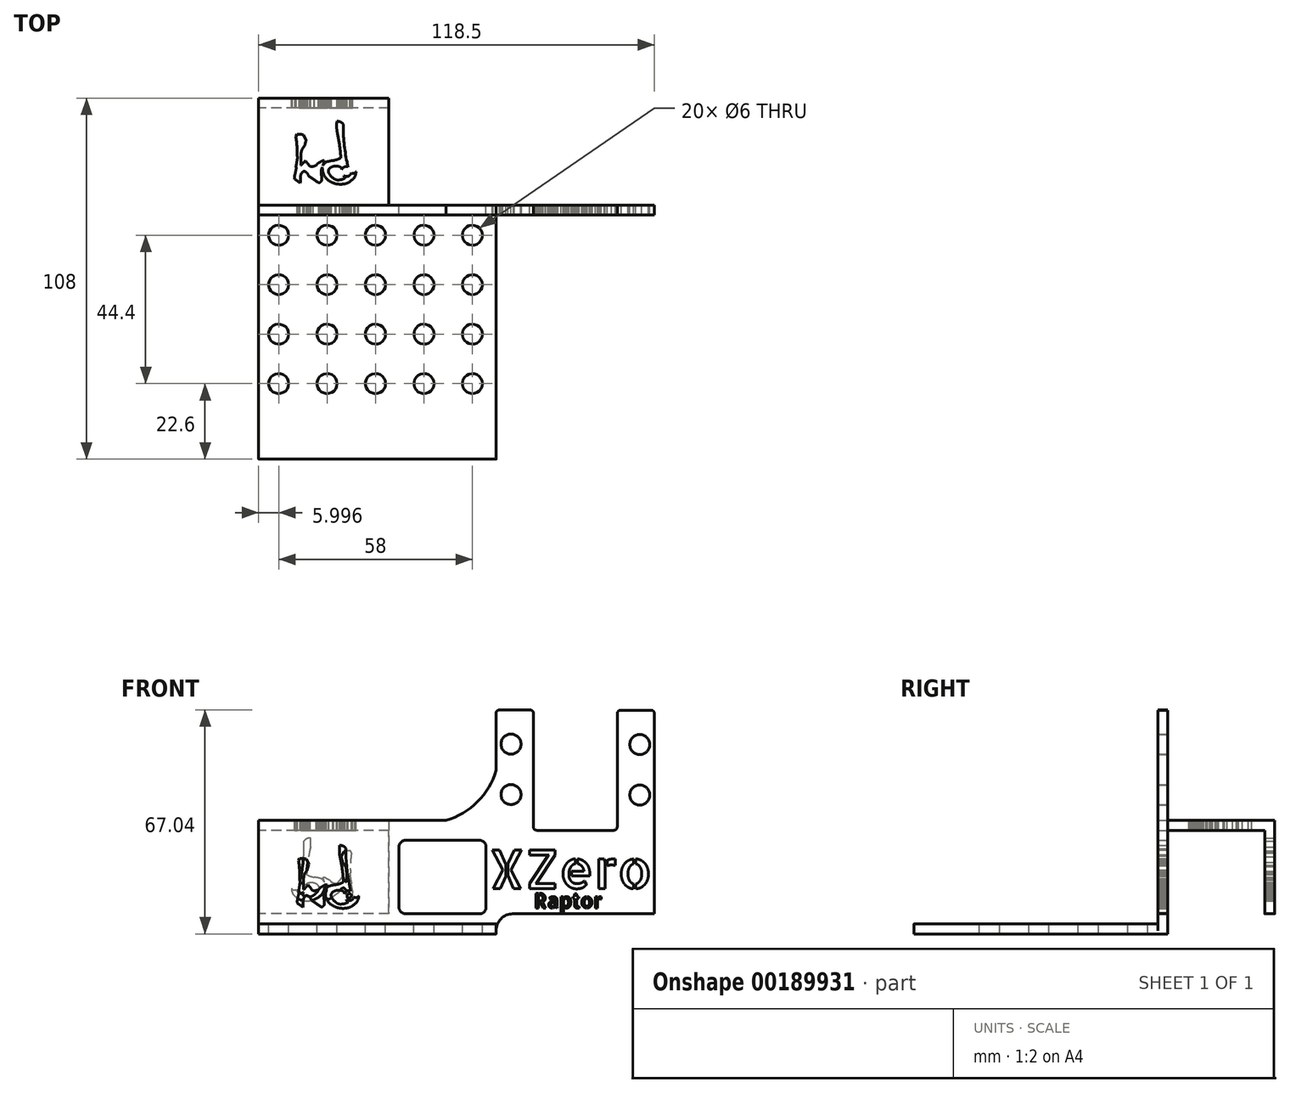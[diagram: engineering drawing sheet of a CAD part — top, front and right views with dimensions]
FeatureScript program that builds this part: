
annotation { "Feature Type Name" : "Feature", "Feature Type Description" : "" }
export const myFeature = defineFeature(function(context is Context, id is Id, definition is map)
    precondition{}
    {
        {
            var Q0;
            Q0=qCreatedBy(makeId("Front.planeOp"),FACE);
            var sketch = newSketch(context, id + "F0", { "sketchPlane" : qUnion([Q0])});
            skLineSegment(sketch, "E0", {"start": v(22.39, 29.47) * mm, "end": v(22.39, 4.47) * mm});
            skLineSegment(sketch, "E1", {"start": v(22.39, 29.47) * mm, "end": v(22.39, 64.37) * mm});
            skLineSegment(sketch, "E2", {"start": v(10.24, 29.47) * mm, "end": v(-12.86, 29.47) * mm});
            skLineSegment(sketch, "E3", {"start": v(-25.01, 47.47) * mm, "end": v(-25.01, 64.5) * mm});
            skLineSegment(sketch, "E4", {"start": v(-25.01, 4.47) * mm, "end": v(22.39, 4.47) * mm});
            skLineSegment(sketch, "E5", {"start": v(-24.01, 65.5) * mm, "end": v(-14.86, 65.5) * mm});
            skLineSegment(sketch, "E6", {"start": v(-13.86, 64.5) * mm, "end": v(-13.86, 30.47) * mm});
            skLineSegment(sketch, "E7", {"start": v(11.24, 64.37) * mm, "end": v(11.24, 30.47) * mm});
            skLineSegment(sketch, "E8", {"start": v(12.24, 65.37) * mm, "end": v(21.39, 65.37) * mm});
            skLineSegment(sketch, "E9", {"start": v(22.39, 2.47) * mm, "end": v(22.39, 4.47) * mm});
            skPoint(sketch, "E10.centerSnap0", {"position": v(-19.44, 65.5) * mm});
            skPoint(sketch, "E11.centerSnap0", {"position": v(16.81, 65.37) * mm});
            skPoint(sketch, "E12.visualSharp", {"position": v(-25.01, 65.5) * mm});
            skArc(sketch, "E12.filletArc", {"start": v(-24.01, 65.5) * mm, "mid": v(-24.72, 65.22) * mm, "end": v(-25.01, 64.5) * mm});
            skPoint(sketch, "E13.visualSharp", {"position": v(-13.86, 65.5) * mm});
            skArc(sketch, "E13.filletArc", {"start": v(-13.86, 64.5) * mm, "mid": v(-14.16, 65.22) * mm, "end": v(-14.86, 65.5) * mm});
            skPoint(sketch, "E14.visualSharp", {"position": v(11.24, 65.37) * mm});
            skArc(sketch, "E14.filletArc", {"start": v(12.24, 65.37) * mm, "mid": v(11.53, 65.08) * mm, "end": v(11.24, 64.37) * mm});
            skPoint(sketch, "E15.visualSharp", {"position": v(22.39, 65.37) * mm});
            skArc(sketch, "E15.filletArc", {"start": v(22.39, 64.37) * mm, "mid": v(22.1, 65.08) * mm, "end": v(21.39, 65.37) * mm});
            skPoint(sketch, "E16.visualSharp", {"position": v(-13.86, 29.47) * mm});
            skArc(sketch, "E16.filletArc", {"start": v(-13.86, 30.47) * mm, "mid": v(-13.57, 29.76) * mm, "end": v(-12.86, 29.47) * mm});
            skPoint(sketch, "E17.visualSharp", {"position": v(11.24, 29.47) * mm});
            skArc(sketch, "E17.filletArc", {"start": v(10.24, 29.47) * mm, "mid": v(10.94, 29.76) * mm, "end": v(11.24, 30.47) * mm});
            skPoint(sketch, "E18.visualSharp", {"position": v(-25.01, 1.47) * mm});
            skPoint(sketch, "E19.visualSharp", {"position": v(22.39, 1.47) * mm});
            skArc(sketch, "E19.filletArc", {"start": v(21.39, 1.47) * mm, "mid": v(22.1, 1.76) * mm, "end": v(22.39, 2.47) * mm});
            skLineSegment(sketch, "E20", {"start": v(-17.56, 55.26) * mm, "end": v(-17.61, 55.26) * mm});
            skLineSegment(sketch, "E21", {"start": v(-23.56, 55.26) * mm, "end": v(-23.51, 55.26) * mm});
            skCircle(sketch, "E22", {"center": v(-20.56, 55.26) * mm, "radius": 3 * mm});
            skCircle(sketch, "E23", {"center": v(17.98, 55.12) * mm, "radius": 3 * mm});
            skPoint(sketch, "E24.end.orphan", {"position": v(20.98, 55.12) * mm});
            skPoint(sketch, "E24.start.orphan", {"position": v(22.39, 55.12) * mm});
            skPoint(sketch, "E25.end.orphan", {"position": v(14.98, 55.12) * mm});
            skPoint(sketch, "E26.orphan", {"position": v(-25.01, 55.26) * mm});
            skCircle(sketch, "E27", {"center": v(-20.56, 40.16) * mm, "radius": 3 * mm});
            skCircle(sketch, "E28", {"center": v(17.98, 40.02) * mm, "radius": 3 * mm});
            skLineSegment(sketch, "E29", {"start": v(-57.11, 29.47) * mm, "end": v(-96.11, 29.47) * mm});
            skLineSegment(sketch, "E30", {"start": v(-96.11, 1.47) * mm, "end": v(-96.11, 29.47) * mm});
            skLineSegment(sketch, "E31.0", {"start": v(-30.01, 4.47) * mm, "end": v(-52.11, 4.47) * mm});
            skLineSegment(sketch, "E31.1", {"start": v(-54.11, 24.47) * mm, "end": v(-54.11, 6.47) * mm});
            skLineSegment(sketch, "E31.2", {"start": v(-30.01, 26.47) * mm, "end": v(-52.11, 26.47) * mm});
            skLineSegment(sketch, "E31.3", {"start": v(-28.01, 24.47) * mm, "end": v(-28.01, 6.47) * mm});
            skLineSegment(sketch, "E32", {"start": v(-96.11, -1.53) * mm, "end": v(-96.11, 1.47) * mm});
            skLineSegment(sketch, "E33", {"start": v(-96.11, 29.47) * mm, "end": v(-96.11, 32.47) * mm});
            skLineSegment(sketch, "E34", {"start": v(-96.11, 32.47) * mm, "end": v(-57.11, 32.47) * mm});
            skLineSegment(sketch, "E35", {"start": v(-57.11, 32.47) * mm, "end": v(-57.11, 29.47) * mm});
            skLineSegment(sketch, "E36", {"start": v(-25.01, 4.47) * mm, "end": v(-25.01, 1.47) * mm});
            skText(sketch, "E37", { "text": "XZero", "fontName": "AllertaStencil-Regular.ttf"});
            skPoint(sketch, "E38.visualSharp", {"position": v(-54.11, 26.47) * mm});
            skArc(sketch, "E38.filletArc", {"start": v(-52.11, 26.47) * mm, "mid": v(-53.53, 25.88) * mm, "end": v(-54.11, 24.47) * mm});
            skPoint(sketch, "E39.visualSharp", {"position": v(-28.01, 26.47) * mm});
            skArc(sketch, "E39.filletArc", {"start": v(-28.01, 24.47) * mm, "mid": v(-28.6, 25.88) * mm, "end": v(-30.01, 26.47) * mm});
            skPoint(sketch, "E40.visualSharp", {"position": v(-54.11, 4.47) * mm});
            skArc(sketch, "E40.filletArc", {"start": v(-54.11, 6.47) * mm, "mid": v(-53.53, 5.05) * mm, "end": v(-52.11, 4.47) * mm});
            skPoint(sketch, "E41.visualSharp", {"position": v(-28.01, 4.47) * mm});
            skArc(sketch, "E41.filletArc", {"start": v(-30.01, 4.47) * mm, "mid": v(-28.6, 5.05) * mm, "end": v(-28.01, 6.47) * mm});
            skLineSegment(sketch, "E42", {"start": v(-25.01, 1.47) * mm, "end": v(-25.01, -1.53) * mm});
            skLineSegment(sketch, "E43", {"start": v(-96.11, -1.53) * mm, "end": v(-25.01, -1.53) * mm});
            skText(sketch, "E44", { "text": "Raptor", "fontName": "AllertaStencil-Regular.ttf"});
            skArc(sketch, "E45", {"start": v(-83.84, 14.55) * mm, "mid": v(-83.85, 17.48) * mm, "end": v(-84.16, 20.4) * mm});
            skLineSegment(sketch, "E46", {"start": v(-84.16, 20.4) * mm, "end": v(-83.84, 21.04) * mm});
            skArc(sketch, "E47", {"start": v(-81.85, 20.88) * mm, "mid": v(-82.84, 21.04) * mm, "end": v(-83.84, 21.04) * mm});
            skLineSegment(sketch, "E48", {"start": v(-81.85, 20.88) * mm, "end": v(-81.1, 19.28) * mm});
            skArc(sketch, "E49", {"start": v(-81.1, 19.28) * mm, "mid": v(-81.32, 18.44) * mm, "end": v(-81.54, 17.6) * mm});
            skArc(sketch, "E50", {"start": v(-81.54, 17.6) * mm, "mid": v(-81.98, 17) * mm, "end": v(-82.38, 16.39) * mm});
            skArc(sketch, "E51", {"start": v(-82.38, 16.39) * mm, "mid": v(-82.56, 15.71) * mm, "end": v(-82.66, 15.02) * mm});
            skArc(sketch, "E52", {"start": v(-82.66, 15.02) * mm, "mid": v(-82.7, 13.37) * mm, "end": v(-82.66, 11.71) * mm});
            skArc(sketch, "E53", {"start": v(-82.66, 11.71) * mm, "mid": v(-81.95, 12.42) * mm, "end": v(-81.29, 13.18) * mm});
            skArc(sketch, "E54", {"start": v(-81.29, 13.18) * mm, "mid": v(-80.58, 12.24) * mm, "end": v(-79.82, 11.34) * mm});
            skArc(sketch, "E55", {"start": v(-79.82, 11.34) * mm, "mid": v(-78.95, 11.45) * mm, "end": v(-78.12, 11.73) * mm});
            skArc(sketch, "E56", {"start": v(-78.12, 11.73) * mm, "mid": v(-77.85, 12) * mm, "end": v(-77.66, 12.34) * mm});
            skArc(sketch, "E57", {"start": v(-77.66, 12.34) * mm, "mid": v(-76.93, 12.71) * mm, "end": v(-76.22, 13.1) * mm});
            skArc(sketch, "E58", {"start": v(-75.6, 13.1) * mm, "mid": v(-75.91, 13.12) * mm, "end": v(-76.22, 13.1) * mm});
            skArc(sketch, "E59", {"start": v(-76.24, 11.3) * mm, "mid": v(-76.41, 10.74) * mm, "end": v(-76.58, 10.16) * mm});
            skArc(sketch, "E60", {"start": v(-76.58, 10.16) * mm, "mid": v(-76.6, 9.55) * mm, "end": v(-76.58, 8.95) * mm});
            skArc(sketch, "E61", {"start": v(-76.58, 8.95) * mm, "mid": v(-76.5, 8.7) * mm, "end": v(-76.42, 8.47) * mm});
            skArc(sketch, "E62", {"start": v(-76.42, 7.43) * mm, "mid": v(-76.42, 7.95) * mm, "end": v(-76.42, 8.47) * mm});
            skArc(sketch, "E63", {"start": v(-76.54, 6.93) * mm, "mid": v(-76.48, 7.18) * mm, "end": v(-76.42, 7.43) * mm});
            skArc(sketch, "E64", {"start": v(-76.54, 6.93) * mm, "mid": v(-76.83, 6.77) * mm, "end": v(-77.06, 6.54) * mm});
            skArc(sketch, "E65", {"start": v(-77.4, 6.54) * mm, "mid": v(-77.23, 6.53) * mm, "end": v(-77.06, 6.54) * mm});
            skArc(sketch, "E66", {"start": v(-77.4, 6.54) * mm, "mid": v(-78.88, 7.58) * mm, "end": v(-80.36, 8.6) * mm});
            skArc(sketch, "E67", {"start": v(-80.36, 8.6) * mm, "mid": v(-80.56, 9.1) * mm, "end": v(-80.83, 9.54) * mm});
            skArc(sketch, "E68", {"start": v(-80.83, 9.54) * mm, "mid": v(-81.28, 9.81) * mm, "end": v(-81.75, 10.07) * mm});
            skArc(sketch, "E69", {"start": v(-81.75, 10.07) * mm, "mid": v(-82.19, 9.66) * mm, "end": v(-82.6, 9.2) * mm});
            skArc(sketch, "E70", {"start": v(-82.6, 9.2) * mm, "mid": v(-82.73, 8.68) * mm, "end": v(-82.78, 8.14) * mm});
            skArc(sketch, "E71", {"start": v(-82.78, 8.14) * mm, "mid": v(-82.8, 7.51) * mm, "end": v(-82.78, 6.89) * mm});
            skArc(sketch, "E72", {"start": v(-82.87, 6.47) * mm, "mid": v(-83.68, 7.07) * mm, "end": v(-84.51, 7.63) * mm});
            skArc(sketch, "E73", {"start": v(-84.51, 8.78) * mm, "mid": v(-84.53, 8.2) * mm, "end": v(-84.51, 7.63) * mm});
            skArc(sketch, "E74", {"start": v(-84.51, 8.78) * mm, "mid": v(-84.2, 10.01) * mm, "end": v(-84, 11.27) * mm});
            skArc(sketch, "E75", {"start": v(-84, 11.27) * mm, "mid": v(-84.08, 11.3) * mm, "end": v(-84.18, 11.33) * mm});
            skArc(sketch, "E76", {"start": v(-84.18, 11.33) * mm, "mid": v(-83.96, 12.28) * mm, "end": v(-83.81, 13.23) * mm});
            skArc(sketch, "E77", {"start": v(-83.84, 14.43) * mm, "mid": v(-83.78, 14.47) * mm, "end": v(-83.72, 14.52) * mm});
            skArc(sketch, "E78", {"start": v(-83.84, 14.43) * mm, "mid": v(-83.84, 14.5) * mm, "end": v(-83.84, 14.55) * mm});
            skArc(sketch, "E79", {"start": v(-83.81, 13.23) * mm, "mid": v(-83.73, 13.63) * mm, "end": v(-83.7, 14.04) * mm});
            skArc(sketch, "E80", {"start": v(-83.7, 14.04) * mm, "mid": v(-83.68, 14.28) * mm, "end": v(-83.72, 14.52) * mm});
            skArc(sketch, "E81", {"start": v(-74.97, 12.78) * mm, "mid": v(-75.16, 12.68) * mm, "end": v(-75.35, 12.56) * mm});
            skArc(sketch, "E82", {"start": v(-73.11, 13.16) * mm, "mid": v(-74.05, 13.02) * mm, "end": v(-74.97, 12.78) * mm});
            skArc(sketch, "E83", {"start": v(-73.11, 13.16) * mm, "mid": v(-71.88, 13.46) * mm, "end": v(-70.72, 13.98) * mm});
            skArc(sketch, "E84", {"start": v(-70.72, 13.98) * mm, "mid": v(-70.8, 15.38) * mm, "end": v(-70.95, 16.77) * mm});
            skArc(sketch, "E85", {"start": v(-70.95, 16.77) * mm, "mid": v(-71.36, 19.48) * mm, "end": v(-71.89, 22.17) * mm});
            skArc(sketch, "E86", {"start": v(-71.89, 24.92) * mm, "mid": v(-71.93, 23.54) * mm, "end": v(-71.89, 22.17) * mm});
            skArc(sketch, "E87", {"start": v(-69.95, 24) * mm, "mid": v(-70.78, 24.74) * mm, "end": v(-71.89, 24.92) * mm});
            skArc(sketch, "E88", {"start": v(-69.95, 24) * mm, "mid": v(-69.73, 18.33) * mm, "end": v(-68.85, 12.74) * mm});
            skArc(sketch, "E89", {"start": v(-68.85, 12.74) * mm, "mid": v(-68.72, 12.01) * mm, "end": v(-68.56, 11.3) * mm});
            skArc(sketch, "E90", {"start": v(-68.56, 11.3) * mm, "mid": v(-69.65, 11.26) * mm, "end": v(-70.44, 10.5) * mm});
            skArc(sketch, "E91", {"start": v(-70.44, 10.5) * mm, "mid": v(-70.63, 11.05) * mm, "end": v(-71.11, 11.38) * mm});
            skArc(sketch, "E92", {"start": v(-71.11, 11.38) * mm, "mid": v(-72.07, 11.53) * mm, "end": v(-73.04, 11.42) * mm});
            skArc(sketch, "E93", {"start": v(-73.04, 11.42) * mm, "mid": v(-73.71, 11.13) * mm, "end": v(-74.25, 10.64) * mm});
            skArc(sketch, "E94", {"start": v(-74.25, 10.64) * mm, "mid": v(-74.43, 10) * mm, "end": v(-74.25, 9.37) * mm});
            skArc(sketch, "E95", {"start": v(-74.25, 9.37) * mm, "mid": v(-73.7, 8.55) * mm, "end": v(-72.95, 7.89) * mm});
            skArc(sketch, "E96", {"start": v(-72.95, 7.89) * mm, "mid": v(-72.37, 7.53) * mm, "end": v(-71.71, 7.35) * mm});
            skArc(sketch, "E97", {"start": v(-71.71, 7.35) * mm, "mid": v(-70.52, 7.5) * mm, "end": v(-69.4, 7.9) * mm});
            skArc(sketch, "E98", {"start": v(-69.84, 8.65) * mm, "mid": v(-69.64, 8.26) * mm, "end": v(-69.4, 7.9) * mm});
            skArc(sketch, "E99", {"start": v(-69.84, 8.65) * mm, "mid": v(-68.52, 8.49) * mm, "end": v(-67.6, 9.45) * mm});
            skArc(sketch, "E100", {"start": v(-67.6, 9.45) * mm, "mid": v(-67.03, 9.35) * mm, "end": v(-66.46, 9.45) * mm});
            skArc(sketch, "E101", {"start": v(-66.46, 9.45) * mm, "mid": v(-66.3, 9.62) * mm, "end": v(-66.19, 9.84) * mm});
            skArc(sketch, "E102", {"start": v(-67.2, 7.52) * mm, "mid": v(-66.42, 8.56) * mm, "end": v(-66.19, 9.84) * mm});
            skArc(sketch, "E103", {"start": v(-69.85, 6.17) * mm, "mid": v(-68.41, 6.62) * mm, "end": v(-67.2, 7.52) * mm});
            skArc(sketch, "E104", {"start": v(-72.92, 6.43) * mm, "mid": v(-71.4, 6.12) * mm, "end": v(-69.85, 6.17) * mm});
            skArc(sketch, "E105", {"start": v(-75.33, 8.1) * mm, "mid": v(-74.22, 7.12) * mm, "end": v(-72.92, 6.43) * mm});
            skLineSegment(sketch, "E106", {"start": v(-82.78, 6.89) * mm, "end": v(-82.87, 6.47) * mm});
            skArc(sketch, "E107", {"start": v(-76.24, 11.3) * mm, "mid": v(-76.03, 9.64) * mm, "end": v(-75.33, 8.1) * mm});
            skArc(sketch, "E108", {"start": v(-75.35, 12.56) * mm, "mid": v(-75.76, 12.16) * mm, "end": v(-76.08, 11.68) * mm});
            skArc(sketch, "E109", {"start": v(-75.6, 13.1) * mm, "mid": v(-75.85, 12.4) * mm, "end": v(-76.08, 11.68) * mm});
            skLineSegment(sketch, "E110", {"start": v(-57.11, 32.47) * mm, "end": v(-40.05, 32.47) * mm});
            skCircle(sketch, "E111.0", {"center": v(-69.01, 9.88) * mm, "radius": 0.65 * mm});
            skArc(sketch, "E112", {"start": v(-40.05, 32.47) * mm, "mid": v(-30.57, 38) * mm, "end": v(-25.01, 47.47) * mm});
            skPoint(sketch, "E113.end.orphan", {"position": v(-25.01, 29.47) * mm});
            skLineSegment(sketch, "E114", {"start": v(-25.01, 1.47) * mm, "end": v(-96.11, 1.47) * mm});
            const initialGuessF0  = {"E37": [-0.02729, 0.012, 1, 0, 0.01158], "E44": [-0.01363, 0.00623, 1, 0, 0.00439]};
            skSetInitialGuess(sketch, initialGuessF0);
            skSolve(sketch);
        }
        {
            var Q0;
            Q0=makeQuery(id+"F0.imprint","IMPRINT",FACE,{"disambiguationData":[TD([[makeQuery(id+"F0.imprint","IMPRINT",EDGE,{"derivedFrom":sQuery(id+"F0.wireOp",EDGE,"E0")}),-1.0]])]});
            var Q1;
            Q1=makeQuery(id+"F0.imprint","IMPRINT",FACE,{"disambiguationData":[TD([[makeQuery(id+"F0.imprint","IMPRINT",EDGE,{"derivedFrom":sQuery(id+"F0.wireOp",EDGE,"E4")}),-1.0]])]});
            var Q2;
            Q2=makeQuery(id+"F0.imprint","IMPRINT",FACE,{"disambiguationData":[TD([[makeQuery(id+"F0.imprint","IMPRINT",EDGE,{"derivedFrom":sQuery(id+"F0.wireOp",EDGE,"E29")}),1.0]])]});
            var Q3;
            {var subQ3=sQuery(id+"F0.wireOp",EDGE,"46Qzlj7U-cznB-aaa3-vZE3-pz9t5rDoRomK");Q3=makeQuery(id+"F0.imprint","IMPRINT",FACE,{"disambiguationData":[TD([[makeQuery(id+"F0.imprint","IMPRINT",EDGE,{"derivedFrom":subQ3}),-1.0]])]});}
            var Q4;
            {var subQ0=sQuery(id+"F0.wireOp",EDGE,"E37.sketch_text.stroke-6");var subQ1=sQuery(id+"F0.wireOp",EDGE,"46Qzlj7U-cznB-aaa3-vZE3-pz9t5rDoRomK");var subQ2=makeQuery(id+"F0.imprint","INTERSECT",VERTEX,{"derivedFrom":[subQ1,subQ0]});Q4=makeQuery(id+"F0.imprint","IMPRINT",FACE,{"disambiguationData":[TD([[makeQuery(id+"F0.imprint","IMPRINT",EDGE,{"disambiguationData":[TD([[subQ2,-1.0]])],"derivedFrom":subQ1}),1.0]])]});}
            var Q5;
            {var subQ0=sQuery(id+"F0.wireOp",EDGE,"idUH9Glq-0qPq-0oZk-nQ6q-rgwbrYVED9FP");Q5=makeQuery(id+"F0.imprint","IMPRINT",FACE,{"disambiguationData":[TD([[makeQuery(id+"F0.imprint","IMPRINT",EDGE,{"derivedFrom":subQ0}),-1.0]])]});}
            extrude(context, id + "F1", {"entities" : qUnion([Q0, Q1, Q2, Q3, Q4, Q5]), "depth" : 3 * mm});
        }
        {
            var Q0;
            Q0=makeQuery(id+"F0.imprint","IMPRINT",FACE,{"disambiguationData":[TD([[makeQuery(id+"F0.imprint","IMPRINT",EDGE,{"derivedFrom":sQuery(id+"F0.wireOp",EDGE,"E29")}),-1.0]])]});
            extrude(context, id + "F2", {"entities" : qUnion([Q0]), "operationType" : NewBodyOperationType.ADD, "depth" : 3 * mm});
        }
        {
            var Q0;
            Q0=makeQuery(id+"F0.imprint","IMPRINT",FACE,{"disambiguationData":[TD([[makeQuery(id+"F0.imprint","IMPRINT",EDGE,{"derivedFrom":sQuery(id+"F0.wireOp",EDGE,"E29")}),-1.0]])]});
            extrude(context, id + "F3", {"entities" : qUnion([Q0]), "oppositeDirection" : true, "depth" : 29 * mm});
        }
        {
            var Q0;
            Q0=makeQuery(id+"F0.imprint","IMPRINT",FACE,{"disambiguationData":[TD([[makeQuery(id+"F0.imprint","IMPRINT",EDGE,{"derivedFrom":sQuery(id+"F0.wireOp",EDGE,"E32")}),-1.0]])]});
            extrude(context, id + "F4", {"entities" : qUnion([Q0]), "operationType" : NewBodyOperationType.ADD, "depth" : 76 * mm});
        }
        {
            var Q0;
            Q0=makeQuery(id+"F3.opExtrude","CAP_FACE",FACE,{"disambiguationData":[OSD([sQuery(id+"F0.wireOp",EDGE,"E29"),sQuery(id+"F0.wireOp",EDGE,"E33"),sQuery(id+"F0.wireOp",EDGE,"E34"),sQuery(id+"F0.wireOp",EDGE,"E35")])],"isStart":false});
            var sketch = newSketch(context, id + "F5", { "sketchPlane" : qUnion([Q0])});
            skLineSegment(sketch, "E115.0", {"start": v(96.11, 32.47) * mm, "end": v(57.11, 32.47) * mm});
            skLineSegment(sketch, "E115.1", {"start": v(57.11, 32.47) * mm, "end": v(57.11, 29.47) * mm});
            skLineSegment(sketch, "E115.2", {"start": v(57.11, 29.47) * mm, "end": v(96.11, 29.47) * mm});
            skLineSegment(sketch, "E115.3", {"start": v(96.11, 29.47) * mm, "end": v(96.11, 32.47) * mm});
            skSolve(sketch);
        }
        {
            var Q0;
            Q0=makeQuery(id+"F5.imprint","IMPRINT",FACE,{"disambiguationData":[TD([[makeQuery(id+"F5.imprint","IMPRINT",EDGE,{"derivedFrom":sQuery(id+"F5.wireOp",EDGE,"E115.0")}),1.0]])]});
            extrude(context, id + "F6", {"entities" : qUnion([Q0]), "operationType" : NewBodyOperationType.ADD, "depth" : 3 * mm});
        }
        {
            var Q0;
            Q0=makeQuery(id+"F6.boolean.opBoolean","MERGE",FACE,{"derivedFrom":[makeQuery(id+"F3.opExtrude","SWEPT_FACE",FACE,{"disambiguationData":[OSD([sQuery(id+"F0.wireOp",EDGE,"E29")])]}),makeQuery(id+"F6.opExtrude","SWEPT_FACE",FACE,{"disambiguationData":[OSD([sQuery(id+"F5.wireOp",EDGE,"E115.2")])]})]});
            var sketch = newSketch(context, id + "F7", { "sketchPlane" : qUnion([Q0])});
            skLineSegment(sketch, "E116", {"start": v(-57.11, -32) * mm, "end": v(-57.11, -29) * mm});
            skLineSegment(sketch, "E117", {"start": v(-57.11, -29) * mm, "end": v(-96.11, -29) * mm});
            skLineSegment(sketch, "E118", {"start": v(-96.11, -29) * mm, "end": v(-96.11, -32) * mm});
            skLineSegment(sketch, "E119", {"start": v(-96.11, -32) * mm, "end": v(-57.11, -32) * mm});
            skSolve(sketch);
        }
        {
            var Q0;
            Q0=makeQuery(id+"F7.imprint","IMPRINT",FACE,{"disambiguationData":[TD([[makeQuery(id+"F7.imprint","IMPRINT",EDGE,{"derivedFrom":sQuery(id+"F7.wireOp",EDGE,"E116")}),1.0]])]});
            extrude(context, id + "F8", {"entities" : qUnion([Q0]), "operationType" : NewBodyOperationType.ADD, "depth" : 25 * mm});
        }
        {
            var Q0;
            Q0=makeQuery(id+"F4.opExtrude","CAP_EDGE",EDGE,{"disambiguationData":[OSD([sQuery(id+"F0.wireOp",EDGE,"E32")])],"isStart":false});
            var Q1;
            Q1=makeQuery(id+"F4.opExtrude","CAP_EDGE",EDGE,{"disambiguationData":[OSD([sQuery(id+"F0.wireOp",EDGE,"dS1XQmwT-nCb9-MQQN-qxri-gYy9wgz1x22k")])],"isStart":false});
            var Q2;
            Q2=makeQuery(id+"F8.opExtrude","CAP_EDGE",EDGE,{"disambiguationData":[OSD([sQuery(id+"F7.wireOp",EDGE,"E118")])],"isStart":false});
            var Q3;
            Q3=makeQuery(id+"F8.opExtrude","CAP_EDGE",EDGE,{"disambiguationData":[OSD([sQuery(id+"F7.wireOp",EDGE,"E116")])],"isStart":false});
            var Q4;
            Q4=makeQuery(id+"F4.opExtrude","CAP_EDGE",EDGE,{"disambiguationData":[OSD([sQuery(id+"F0.wireOp",EDGE,"mx6WqFKt-vM0y-SFEN-eErL-Z0JPfcJ78krc")])],"isStart":true});
            var Q5;
            Q5=makeQuery(id+"F4.opExtrude","CAP_EDGE",EDGE,{"disambiguationData":[OSD([sQuery(id+"F0.wireOp",EDGE,"E36"),sQuery(id+"F0.wireOp",EDGE,"E42")])],"isStart":false});
            var Q6;
            Q6=makeQuery(id+"F1.opExtrude","SWEPT_EDGE",EDGE,{"disambiguationData":[OSD([sQuery(id+"F0.wireOp",EDGE,"E3"),sQuery(id+"F0.wireOp",EDGE,"46Qzlj7U-cznB-aaa3-vZE3-pz9t5rDoRomK"),sQuery(id+"F0.wireOp",EDGE,"idUH9Glq-0qPq-0oZk-nQ6q-rgwbrYVED9FP")])]});
            fillet(context, id + "F9", {"entities" : qUnion([Q0, Q1, Q2, Q3, Q4, Q5, Q6]), "radius" : 0.02 * mm, "tangentPropagation" : true, "allowEdgeOverflow" : false});
        }
        {
            var Q0;
            Q0=makeQuery(id+"F4.opExtrude","SWEPT_FACE",FACE,{"disambiguationData":[OSD([sQuery(id+"F0.wireOp",EDGE,"E114")])]});
            var sketch = newSketch(context, id + "F10", { "sketchPlane" : qUnion([Q0])});
            skCircle(sketch, "E120", {"center": v(-90.11, -9) * mm, "radius": 3 * mm});
            skCircle(sketch, "E121.0.1.0", {"center": v(-90.11, -23.8) * mm, "radius": 3 * mm});
            skCircle(sketch, "E121.0.2.0", {"center": v(-90.11, -38.6) * mm, "radius": 3 * mm});
            skCircle(sketch, "E121.0.3.0", {"center": v(-90.11, -53.4) * mm, "radius": 3 * mm});
            skCircle(sketch, "E121.0.4.0", {"center": v(-90.11, -68.2) * mm, "radius": 3 * mm});
            skCircle(sketch, "E121.1.0.0", {"center": v(-75.61, -9) * mm, "radius": 3 * mm});
            skCircle(sketch, "E121.1.1.0", {"center": v(-75.61, -23.8) * mm, "radius": 3 * mm});
            skCircle(sketch, "E121.1.2.0", {"center": v(-75.61, -38.6) * mm, "radius": 3 * mm});
            skCircle(sketch, "E121.1.3.0", {"center": v(-75.61, -53.4) * mm, "radius": 3 * mm});
            skCircle(sketch, "E121.1.4.0", {"center": v(-75.61, -68.2) * mm, "radius": 3 * mm});
            skCircle(sketch, "E121.2.0.0", {"center": v(-61.11, -9) * mm, "radius": 3 * mm});
            skCircle(sketch, "E121.2.1.0", {"center": v(-61.11, -23.8) * mm, "radius": 3 * mm});
            skCircle(sketch, "E121.2.2.0", {"center": v(-61.11, -38.6) * mm, "radius": 3 * mm});
            skCircle(sketch, "E121.2.3.0", {"center": v(-61.11, -53.4) * mm, "radius": 3 * mm});
            skCircle(sketch, "E121.2.4.0", {"center": v(-61.11, -68.2) * mm, "radius": 3 * mm});
            skCircle(sketch, "E121.3.0.0", {"center": v(-46.61, -9) * mm, "radius": 3 * mm});
            skCircle(sketch, "E121.3.1.0", {"center": v(-46.61, -23.8) * mm, "radius": 3 * mm});
            skCircle(sketch, "E121.3.2.0", {"center": v(-46.61, -38.6) * mm, "radius": 3 * mm});
            skCircle(sketch, "E121.3.3.0", {"center": v(-46.61, -53.4) * mm, "radius": 3 * mm});
            skCircle(sketch, "E121.3.4.0", {"center": v(-46.61, -68.2) * mm, "radius": 3 * mm});
            skCircle(sketch, "E121.4.0.0", {"center": v(-32.11, -9) * mm, "radius": 3 * mm});
            skCircle(sketch, "E121.4.1.0", {"center": v(-32.11, -23.8) * mm, "radius": 3 * mm});
            skCircle(sketch, "E121.4.2.0", {"center": v(-32.11, -38.6) * mm, "radius": 3 * mm});
            skCircle(sketch, "E121.4.3.0", {"center": v(-32.11, -53.4) * mm, "radius": 3 * mm});
            skCircle(sketch, "E121.4.4.0", {"center": v(-32.11, -68.2) * mm, "radius": 3 * mm});
            skLineSegment(sketch, "E121.direction1", {"start": v(-90.11, -9) * mm, "end": v(-75.61, -9) * mm, "construction": true});
            skLineSegment(sketch, "E121.direction2", {"start": v(-90.11, -9) * mm, "end": v(-90.11, -23.8) * mm, "construction": true});
            skSolve(sketch);
        }
        {
            var Q0;
            Q0=makeQuery(id+"F6.boolean.opBoolean","MERGE",FACE,{"derivedFrom":[makeQuery(id+"F3.opExtrude","SWEPT_FACE",FACE,{"disambiguationData":[OSD([sQuery(id+"F0.wireOp",EDGE,"E34")])]}),makeQuery(id+"F6.opExtrude","SWEPT_FACE",FACE,{"disambiguationData":[OSD([sQuery(id+"F5.wireOp",EDGE,"E115.0")])]})]});
            var sketch = newSketch(context, id + "F11", { "sketchPlane" : qUnion([Q0])});
            skArc(sketch, "E122", {"start": v(-84.64, 14.69) * mm, "mid": v(-84.65, 17.62) * mm, "end": v(-84.97, 20.53) * mm});
            skLineSegment(sketch, "E123", {"start": v(-84.97, 20.53) * mm, "end": v(-84.64, 21.18) * mm});
            skArc(sketch, "E124", {"start": v(-82.65, 21.01) * mm, "mid": v(-83.64, 21.18) * mm, "end": v(-84.64, 21.18) * mm});
            skLineSegment(sketch, "E125", {"start": v(-82.65, 21.01) * mm, "end": v(-81.9, 19.41) * mm});
            skArc(sketch, "E126", {"start": v(-81.9, 19.41) * mm, "mid": v(-82.12, 18.58) * mm, "end": v(-82.35, 17.74) * mm});
            skArc(sketch, "E127", {"start": v(-82.35, 17.74) * mm, "mid": v(-82.78, 17.14) * mm, "end": v(-83.18, 16.53) * mm});
            skArc(sketch, "E128", {"start": v(-83.18, 16.53) * mm, "mid": v(-83.36, 15.85) * mm, "end": v(-83.46, 15.16) * mm});
            skArc(sketch, "E129", {"start": v(-83.46, 15.16) * mm, "mid": v(-83.5, 13.5) * mm, "end": v(-83.46, 11.85) * mm});
            skArc(sketch, "E130", {"start": v(-83.46, 11.85) * mm, "mid": v(-82.75, 12.56) * mm, "end": v(-82.1, 13.32) * mm});
            skArc(sketch, "E131", {"start": v(-82.1, 13.32) * mm, "mid": v(-81.39, 12.37) * mm, "end": v(-80.62, 11.48) * mm});
            skArc(sketch, "E132", {"start": v(-80.62, 11.48) * mm, "mid": v(-79.75, 11.59) * mm, "end": v(-78.93, 11.87) * mm});
            skArc(sketch, "E133", {"start": v(-78.93, 11.87) * mm, "mid": v(-78.66, 12.15) * mm, "end": v(-78.46, 12.48) * mm});
            skArc(sketch, "E134", {"start": v(-78.46, 12.48) * mm, "mid": v(-77.73, 12.85) * mm, "end": v(-77.02, 13.25) * mm});
            skArc(sketch, "E135", {"start": v(-76.4, 13.25) * mm, "mid": v(-76.71, 13.26) * mm, "end": v(-77.02, 13.25) * mm});
            skArc(sketch, "E136", {"start": v(-77.04, 11.44) * mm, "mid": v(-77.22, 10.87) * mm, "end": v(-77.38, 10.3) * mm});
            skArc(sketch, "E137", {"start": v(-77.38, 10.3) * mm, "mid": v(-77.41, 9.7) * mm, "end": v(-77.38, 9.08) * mm});
            skArc(sketch, "E138", {"start": v(-77.38, 9.08) * mm, "mid": v(-77.3, 8.85) * mm, "end": v(-77.22, 8.6) * mm});
            skArc(sketch, "E139", {"start": v(-77.22, 7.57) * mm, "mid": v(-77.22, 8.1) * mm, "end": v(-77.22, 8.6) * mm});
            skArc(sketch, "E140", {"start": v(-77.35, 7.07) * mm, "mid": v(-77.28, 7.32) * mm, "end": v(-77.22, 7.57) * mm});
            skArc(sketch, "E141", {"start": v(-77.35, 7.07) * mm, "mid": v(-77.63, 6.9) * mm, "end": v(-77.86, 6.68) * mm});
            skArc(sketch, "E142", {"start": v(-78.2, 6.68) * mm, "mid": v(-78.04, 6.66) * mm, "end": v(-77.86, 6.68) * mm});
            skArc(sketch, "E143", {"start": v(-78.2, 6.68) * mm, "mid": v(-79.68, 7.72) * mm, "end": v(-81.16, 8.74) * mm});
            skArc(sketch, "E144", {"start": v(-81.16, 8.74) * mm, "mid": v(-81.36, 9.23) * mm, "end": v(-81.63, 9.68) * mm});
            skArc(sketch, "E145", {"start": v(-81.63, 9.68) * mm, "mid": v(-82.09, 9.95) * mm, "end": v(-82.55, 10.2) * mm});
            skArc(sketch, "E146", {"start": v(-82.55, 10.2) * mm, "mid": v(-83, 9.8) * mm, "end": v(-83.4, 9.35) * mm});
            skArc(sketch, "E147", {"start": v(-83.4, 9.35) * mm, "mid": v(-83.53, 8.82) * mm, "end": v(-83.58, 8.28) * mm});
            skArc(sketch, "E148", {"start": v(-83.58, 8.28) * mm, "mid": v(-83.6, 7.65) * mm, "end": v(-83.58, 7.02) * mm});
            skArc(sketch, "E149", {"start": v(-83.67, 6.6) * mm, "mid": v(-84.48, 7.2) * mm, "end": v(-85.32, 7.76) * mm});
            skArc(sketch, "E150", {"start": v(-85.32, 8.92) * mm, "mid": v(-85.33, 8.34) * mm, "end": v(-85.32, 7.76) * mm});
            skArc(sketch, "E151", {"start": v(-85.32, 8.92) * mm, "mid": v(-85, 10.15) * mm, "end": v(-84.8, 11.4) * mm});
            skArc(sketch, "E152", {"start": v(-84.8, 11.4) * mm, "mid": v(-84.88, 11.44) * mm, "end": v(-84.98, 11.47) * mm});
            skArc(sketch, "E153", {"start": v(-84.98, 11.47) * mm, "mid": v(-84.77, 12.41) * mm, "end": v(-84.62, 13.37) * mm});
            skArc(sketch, "E154", {"start": v(-84.64, 14.57) * mm, "mid": v(-84.58, 14.6) * mm, "end": v(-84.53, 14.65) * mm});
            skArc(sketch, "E155", {"start": v(-84.64, 14.57) * mm, "mid": v(-84.64, 14.63) * mm, "end": v(-84.64, 14.69) * mm});
            skArc(sketch, "E156", {"start": v(-84.62, 13.37) * mm, "mid": v(-84.53, 13.77) * mm, "end": v(-84.5, 14.17) * mm});
            skArc(sketch, "E157", {"start": v(-84.5, 14.17) * mm, "mid": v(-84.48, 14.41) * mm, "end": v(-84.53, 14.65) * mm});
            skArc(sketch, "E158", {"start": v(-75.77, 12.92) * mm, "mid": v(-75.97, 12.82) * mm, "end": v(-76.15, 12.7) * mm});
            skArc(sketch, "E159", {"start": v(-73.92, 13.3) * mm, "mid": v(-74.86, 13.16) * mm, "end": v(-75.77, 12.92) * mm});
            skArc(sketch, "E160", {"start": v(-73.92, 13.3) * mm, "mid": v(-72.68, 13.6) * mm, "end": v(-71.52, 14.11) * mm});
            skArc(sketch, "E161", {"start": v(-71.52, 14.11) * mm, "mid": v(-71.6, 15.52) * mm, "end": v(-71.75, 16.91) * mm});
            skArc(sketch, "E162", {"start": v(-71.75, 16.91) * mm, "mid": v(-72.16, 19.62) * mm, "end": v(-72.69, 22.3) * mm});
            skArc(sketch, "E163", {"start": v(-72.69, 25.05) * mm, "mid": v(-72.73, 23.68) * mm, "end": v(-72.69, 22.3) * mm});
            skArc(sketch, "E164", {"start": v(-70.76, 24.13) * mm, "mid": v(-71.59, 24.87) * mm, "end": v(-72.69, 25.05) * mm});
            skArc(sketch, "E165", {"start": v(-70.76, 24.13) * mm, "mid": v(-70.53, 18.47) * mm, "end": v(-69.66, 12.87) * mm});
            skArc(sketch, "E166", {"start": v(-69.66, 12.87) * mm, "mid": v(-69.52, 12.15) * mm, "end": v(-69.36, 11.43) * mm});
            skArc(sketch, "E167", {"start": v(-69.36, 11.43) * mm, "mid": v(-70.45, 11.4) * mm, "end": v(-71.25, 10.65) * mm});
            skArc(sketch, "E168", {"start": v(-71.25, 10.65) * mm, "mid": v(-71.44, 11.19) * mm, "end": v(-71.91, 11.51) * mm});
            skArc(sketch, "E169", {"start": v(-71.91, 11.51) * mm, "mid": v(-72.88, 11.67) * mm, "end": v(-73.84, 11.56) * mm});
            skArc(sketch, "E170", {"start": v(-73.84, 11.56) * mm, "mid": v(-74.51, 11.27) * mm, "end": v(-75.06, 10.78) * mm});
            skArc(sketch, "E171", {"start": v(-75.06, 10.78) * mm, "mid": v(-75.24, 10.14) * mm, "end": v(-75.06, 9.5) * mm});
            skArc(sketch, "E172", {"start": v(-75.06, 9.5) * mm, "mid": v(-74.5, 8.68) * mm, "end": v(-73.75, 8.02) * mm});
            skArc(sketch, "E173", {"start": v(-73.75, 8.02) * mm, "mid": v(-73.17, 7.66) * mm, "end": v(-72.51, 7.49) * mm});
            skArc(sketch, "E174", {"start": v(-72.51, 7.49) * mm, "mid": v(-71.33, 7.63) * mm, "end": v(-70.2, 8.03) * mm});
            skArc(sketch, "E175", {"start": v(-70.64, 8.8) * mm, "mid": v(-70.44, 8.4) * mm, "end": v(-70.2, 8.03) * mm});
            skArc(sketch, "E176", {"start": v(-70.64, 8.8) * mm, "mid": v(-69.32, 8.62) * mm, "end": v(-68.4, 9.59) * mm});
            skArc(sketch, "E177", {"start": v(-68.4, 9.59) * mm, "mid": v(-67.83, 9.5) * mm, "end": v(-67.27, 9.59) * mm});
            skArc(sketch, "E178", {"start": v(-67.27, 9.59) * mm, "mid": v(-67.1, 9.76) * mm, "end": v(-66.99, 9.97) * mm});
            skArc(sketch, "E179", {"start": v(-68, 7.66) * mm, "mid": v(-67.22, 8.7) * mm, "end": v(-66.99, 9.97) * mm});
            skArc(sketch, "E180", {"start": v(-70.65, 6.3) * mm, "mid": v(-69.22, 6.76) * mm, "end": v(-68, 7.66) * mm});
            skArc(sketch, "E181", {"start": v(-73.72, 6.57) * mm, "mid": v(-72.2, 6.26) * mm, "end": v(-70.65, 6.3) * mm});
            skArc(sketch, "E182", {"start": v(-76.13, 8.24) * mm, "mid": v(-75.03, 7.26) * mm, "end": v(-73.72, 6.57) * mm});
            skLineSegment(sketch, "E183", {"start": v(-83.58, 7.02) * mm, "end": v(-83.67, 6.6) * mm});
            skArc(sketch, "E184", {"start": v(-75.77, 12.92) * mm, "mid": v(-75.97, 12.81) * mm, "end": v(-76.15, 12.7) * mm});
            skArc(sketch, "E185", {"start": v(-77.04, 11.44) * mm, "mid": v(-76.83, 9.77) * mm, "end": v(-76.13, 8.24) * mm});
            skArc(sketch, "E186", {"start": v(-76.15, 12.7) * mm, "mid": v(-76.56, 12.3) * mm, "end": v(-76.89, 11.82) * mm});
            skArc(sketch, "E187", {"start": v(-76.4, 13.25) * mm, "mid": v(-76.65, 12.53) * mm, "end": v(-76.89, 11.82) * mm});
            skCircle(sketch, "E188.0", {"center": v(-69.81, 10.02) * mm, "radius": 0.65 * mm});
            skSolve(sketch);
        }
        {
            var Q0;
            Q0=makeQuery(id+"F11.imprint","IMPRINT",FACE,{"disambiguationData":[TD([[makeQuery(id+"F11.imprint","IMPRINT",EDGE,{"derivedFrom":sQuery(id+"F11.wireOp",EDGE,"E122")}),-1.0]])]});
            var Q1;
            Q1=makeQuery(id+"F11.imprint","IMPRINT",FACE,{"disambiguationData":[TD([[makeQuery(id+"F11.imprint","IMPRINT",EDGE,{"derivedFrom":sQuery(id+"F11.wireOp",EDGE,"e9a27ff7-29ba-4c5a-bb0c-0f35ec83b421")}),1.0]])]});
            extrude(context, id + "F12", {"entities" : qUnion([Q0, Q1]), "operationType" : NewBodyOperationType.REMOVE, "oppositeDirection" : true, "depth" : 3 * mm});
        }
        {
            var Q0;
            Q0=makeQuery(id+"F10.imprint","IMPRINT",FACE,{"disambiguationData":[TD([[makeQuery(id+"F10.imprint","IMPRINT",EDGE,{"derivedFrom":sQuery(id+"F10.wireOp",EDGE,"E120")}),1.0]])]});
            var Q1;
            Q1=makeQuery(id+"F10.imprint","IMPRINT",FACE,{"disambiguationData":[TD([[makeQuery(id+"F10.imprint","IMPRINT",EDGE,{"derivedFrom":sQuery(id+"F10.wireOp",EDGE,"E121.1.0.0")}),1.0]])]});
            var Q2;
            Q2=makeQuery(id+"F10.imprint","IMPRINT",FACE,{"disambiguationData":[TD([[makeQuery(id+"F10.imprint","IMPRINT",EDGE,{"derivedFrom":sQuery(id+"F10.wireOp",EDGE,"E121.2.0.0")}),1.0]])]});
            var Q3;
            Q3=makeQuery(id+"F10.imprint","IMPRINT",FACE,{"disambiguationData":[TD([[makeQuery(id+"F10.imprint","IMPRINT",EDGE,{"derivedFrom":sQuery(id+"F10.wireOp",EDGE,"E121.4.0.0")}),1.0]])]});
            var Q4;
            Q4=makeQuery(id+"F10.imprint","IMPRINT",FACE,{"disambiguationData":[TD([[makeQuery(id+"F10.imprint","IMPRINT",EDGE,{"derivedFrom":sQuery(id+"F10.wireOp",EDGE,"E121.4.1.0")}),1.0]])]});
            var Q5;
            Q5=makeQuery(id+"F10.imprint","IMPRINT",FACE,{"disambiguationData":[TD([[makeQuery(id+"F10.imprint","IMPRINT",EDGE,{"derivedFrom":sQuery(id+"F10.wireOp",EDGE,"E121.3.1.0")}),1.0]])]});
            var Q6;
            Q6=makeQuery(id+"F10.imprint","IMPRINT",FACE,{"disambiguationData":[TD([[makeQuery(id+"F10.imprint","IMPRINT",EDGE,{"derivedFrom":sQuery(id+"F10.wireOp",EDGE,"E121.3.2.0")}),1.0]])]});
            var Q7;
            Q7=makeQuery(id+"F10.imprint","IMPRINT",FACE,{"disambiguationData":[TD([[makeQuery(id+"F10.imprint","IMPRINT",EDGE,{"derivedFrom":sQuery(id+"F10.wireOp",EDGE,"E121.4.2.0")}),1.0]])]});
            var Q8;
            Q8=makeQuery(id+"F10.imprint","IMPRINT",FACE,{"disambiguationData":[TD([[makeQuery(id+"F10.imprint","IMPRINT",EDGE,{"derivedFrom":sQuery(id+"F10.wireOp",EDGE,"E121.4.3.0")}),1.0]])]});
            var Q9;
            Q9=makeQuery(id+"F10.imprint","IMPRINT",FACE,{"disambiguationData":[TD([[makeQuery(id+"F10.imprint","IMPRINT",EDGE,{"derivedFrom":sQuery(id+"F10.wireOp",EDGE,"E121.3.3.0")}),1.0]])]});
            var Q10;
            Q10=makeQuery(id+"F10.imprint","IMPRINT",FACE,{"disambiguationData":[TD([[makeQuery(id+"F10.imprint","IMPRINT",EDGE,{"derivedFrom":sQuery(id+"F10.wireOp",EDGE,"E121.2.3.0")}),1.0]])]});
            var Q11;
            Q11=makeQuery(id+"F10.imprint","IMPRINT",FACE,{"disambiguationData":[TD([[makeQuery(id+"F10.imprint","IMPRINT",EDGE,{"derivedFrom":sQuery(id+"F10.wireOp",EDGE,"E121.2.2.0")}),1.0]])]});
            var Q12;
            Q12=makeQuery(id+"F10.imprint","IMPRINT",FACE,{"disambiguationData":[TD([[makeQuery(id+"F10.imprint","IMPRINT",EDGE,{"derivedFrom":sQuery(id+"F10.wireOp",EDGE,"E121.2.1.0")}),1.0]])]});
            var Q13;
            Q13=makeQuery(id+"F10.imprint","IMPRINT",FACE,{"disambiguationData":[TD([[makeQuery(id+"F10.imprint","IMPRINT",EDGE,{"derivedFrom":sQuery(id+"F10.wireOp",EDGE,"E121.1.1.0")}),1.0]])]});
            var Q14;
            Q14=makeQuery(id+"F10.imprint","IMPRINT",FACE,{"disambiguationData":[TD([[makeQuery(id+"F10.imprint","IMPRINT",EDGE,{"derivedFrom":sQuery(id+"F10.wireOp",EDGE,"E121.1.2.0")}),1.0]])]});
            var Q15;
            Q15=makeQuery(id+"F10.imprint","IMPRINT",FACE,{"disambiguationData":[TD([[makeQuery(id+"F10.imprint","IMPRINT",EDGE,{"derivedFrom":sQuery(id+"F10.wireOp",EDGE,"E121.1.3.0")}),1.0]])]});
            var Q16;
            Q16=makeQuery(id+"F10.imprint","IMPRINT",FACE,{"disambiguationData":[TD([[makeQuery(id+"F10.imprint","IMPRINT",EDGE,{"derivedFrom":sQuery(id+"F10.wireOp",EDGE,"E121.0.3.0")}),1.0]])]});
            var Q17;
            Q17=makeQuery(id+"F10.imprint","IMPRINT",FACE,{"disambiguationData":[TD([[makeQuery(id+"F10.imprint","IMPRINT",EDGE,{"derivedFrom":sQuery(id+"F10.wireOp",EDGE,"E121.0.2.0")}),1.0]])]});
            var Q18;
            Q18=makeQuery(id+"F10.imprint","IMPRINT",FACE,{"disambiguationData":[TD([[makeQuery(id+"F10.imprint","IMPRINT",EDGE,{"derivedFrom":sQuery(id+"F10.wireOp",EDGE,"E121.0.1.0")}),1.0]])]});
            var Q19;
            Q19=makeQuery(id+"F10.imprint","IMPRINT",FACE,{"disambiguationData":[TD([[makeQuery(id+"F10.imprint","IMPRINT",EDGE,{"derivedFrom":sQuery(id+"F10.wireOp",EDGE,"E121.3.0.0")}),1.0]])]});
            extrude(context, id + "F13", {"entities" : qUnion([Q0, Q1, Q2, Q3, Q4, Q5, Q6, Q7, Q8, Q9, Q10, Q11, Q12, Q13, Q14, Q15, Q16, Q17, Q18, Q19]), "operationType" : NewBodyOperationType.REMOVE, "oppositeDirection" : true, "depth" : 3 * mm});
        }
        {
            var Q0;
            Q0=makeQuery(id+"F8.boolean.opBoolean","MERGE",FACE,{"derivedFrom":[makeQuery(id+"F6.opExtrude","CAP_FACE",FACE,{"disambiguationData":[OSD([sQuery(id+"F5.wireOp",EDGE,"E115.0"),sQuery(id+"F5.wireOp",EDGE,"E115.1"),sQuery(id+"F5.wireOp",EDGE,"E115.2"),sQuery(id+"F5.wireOp",EDGE,"E115.3")])],"isStart":false}),makeQuery(id+"F8.opExtrude","SWEPT_FACE",FACE,{"disambiguationData":[OSD([sQuery(id+"F7.wireOp",EDGE,"E119")])]})]});
            var sketch = newSketch(context, id + "F14", { "sketchPlane" : qUnion([Q0])});
            skArc(sketch, "E189", {"start": v(68.62, 16.8) * mm, "mid": v(68.62, 19.72) * mm, "end": v(68.3, 22.63) * mm});
            skLineSegment(sketch, "E190", {"start": v(68.3, 22.63) * mm, "end": v(68.63, 23.28) * mm});
            skArc(sketch, "E191", {"start": v(70.61, 23.12) * mm, "mid": v(69.63, 23.28) * mm, "end": v(68.63, 23.28) * mm});
            skLineSegment(sketch, "E192", {"start": v(70.61, 23.12) * mm, "end": v(71.37, 21.52) * mm});
            skArc(sketch, "E193", {"start": v(71.37, 21.52) * mm, "mid": v(71.15, 20.68) * mm, "end": v(70.92, 19.84) * mm});
            skArc(sketch, "E194", {"start": v(70.92, 19.84) * mm, "mid": v(70.49, 19.25) * mm, "end": v(70.09, 18.63) * mm});
            skArc(sketch, "E195", {"start": v(70.09, 18.63) * mm, "mid": v(69.9, 17.95) * mm, "end": v(69.8, 17.26) * mm});
            skArc(sketch, "E196", {"start": v(69.8, 17.26) * mm, "mid": v(69.77, 15.6) * mm, "end": v(69.8, 13.96) * mm});
            skArc(sketch, "E197", {"start": v(69.8, 13.96) * mm, "mid": v(70.51, 14.67) * mm, "end": v(71.18, 15.42) * mm});
            skArc(sketch, "E198", {"start": v(71.18, 15.42) * mm, "mid": v(71.88, 14.48) * mm, "end": v(72.65, 13.58) * mm});
            skArc(sketch, "E199", {"start": v(72.65, 13.58) * mm, "mid": v(73.51, 13.7) * mm, "end": v(74.34, 13.98) * mm});
            skArc(sketch, "E200", {"start": v(74.34, 13.98) * mm, "mid": v(74.61, 14.25) * mm, "end": v(74.8, 14.58) * mm});
            skArc(sketch, "E201", {"start": v(74.8, 14.58) * mm, "mid": v(75.53, 14.96) * mm, "end": v(76.25, 15.35) * mm});
            skArc(sketch, "E202", {"start": v(76.86, 15.35) * mm, "mid": v(76.55, 15.36) * mm, "end": v(76.25, 15.35) * mm});
            skArc(sketch, "E203", {"start": v(76.23, 13.55) * mm, "mid": v(76.05, 12.98) * mm, "end": v(75.88, 12.4) * mm});
            skArc(sketch, "E204", {"start": v(75.88, 12.4) * mm, "mid": v(75.86, 11.8) * mm, "end": v(75.88, 11.19) * mm});
            skArc(sketch, "E205", {"start": v(75.88, 11.19) * mm, "mid": v(75.96, 10.95) * mm, "end": v(76.04, 10.71) * mm});
            skArc(sketch, "E206", {"start": v(76.04, 9.68) * mm, "mid": v(76.05, 10.2) * mm, "end": v(76.04, 10.71) * mm});
            skArc(sketch, "E207", {"start": v(75.92, 9.17) * mm, "mid": v(75.99, 9.42) * mm, "end": v(76.04, 9.68) * mm});
            skArc(sketch, "E208", {"start": v(75.92, 9.17) * mm, "mid": v(75.63, 9.01) * mm, "end": v(75.4, 8.78) * mm});
            skArc(sketch, "E209", {"start": v(75.06, 8.78) * mm, "mid": v(75.23, 8.77) * mm, "end": v(75.4, 8.78) * mm});
            skArc(sketch, "E210", {"start": v(75.06, 8.78) * mm, "mid": v(73.59, 9.82) * mm, "end": v(72.1, 10.85) * mm});
            skArc(sketch, "E211", {"start": v(72.1, 10.85) * mm, "mid": v(71.9, 11.33) * mm, "end": v(71.63, 11.78) * mm});
            skArc(sketch, "E212", {"start": v(71.63, 11.78) * mm, "mid": v(71.18, 12.06) * mm, "end": v(70.71, 12.3) * mm});
            skArc(sketch, "E213", {"start": v(70.71, 12.3) * mm, "mid": v(70.27, 11.9) * mm, "end": v(69.87, 11.45) * mm});
            skArc(sketch, "E214", {"start": v(69.87, 11.45) * mm, "mid": v(69.73, 10.93) * mm, "end": v(69.68, 10.38) * mm});
            skArc(sketch, "E215", {"start": v(69.68, 10.38) * mm, "mid": v(69.67, 9.76) * mm, "end": v(69.68, 9.13) * mm});
            skArc(sketch, "E216", {"start": v(69.6, 8.71) * mm, "mid": v(68.78, 9.3) * mm, "end": v(67.95, 9.87) * mm});
            skArc(sketch, "E217", {"start": v(67.95, 11.02) * mm, "mid": v(67.94, 10.44) * mm, "end": v(67.95, 9.87) * mm});
            skArc(sketch, "E218", {"start": v(67.95, 11.02) * mm, "mid": v(68.26, 12.26) * mm, "end": v(68.47, 13.51) * mm});
            skArc(sketch, "E219", {"start": v(68.47, 13.51) * mm, "mid": v(68.38, 13.55) * mm, "end": v(68.29, 13.58) * mm});
            skArc(sketch, "E220", {"start": v(68.29, 13.58) * mm, "mid": v(68.5, 14.52) * mm, "end": v(68.65, 15.47) * mm});
            skArc(sketch, "E221", {"start": v(68.62, 16.67) * mm, "mid": v(68.68, 16.71) * mm, "end": v(68.74, 16.76) * mm});
            skArc(sketch, "E222", {"start": v(68.62, 16.67) * mm, "mid": v(68.62, 16.73) * mm, "end": v(68.62, 16.8) * mm});
            skArc(sketch, "E223", {"start": v(68.65, 15.47) * mm, "mid": v(68.73, 15.87) * mm, "end": v(68.77, 16.28) * mm});
            skArc(sketch, "E224", {"start": v(68.77, 16.28) * mm, "mid": v(68.78, 16.52) * mm, "end": v(68.74, 16.76) * mm});
            skArc(sketch, "E225", {"start": v(77.5, 15.02) * mm, "mid": v(77.3, 14.92) * mm, "end": v(77.12, 14.8) * mm});
            skArc(sketch, "E226", {"start": v(79.35, 15.4) * mm, "mid": v(78.41, 15.27) * mm, "end": v(77.5, 15.02) * mm});
            skArc(sketch, "E227", {"start": v(79.35, 15.4) * mm, "mid": v(80.59, 15.7) * mm, "end": v(81.74, 16.22) * mm});
            skArc(sketch, "E228", {"start": v(81.74, 16.22) * mm, "mid": v(81.67, 17.62) * mm, "end": v(81.51, 19.02) * mm});
            skArc(sketch, "E229", {"start": v(81.51, 19.02) * mm, "mid": v(81.1, 21.73) * mm, "end": v(80.58, 24.41) * mm});
            skArc(sketch, "E230", {"start": v(80.58, 27.16) * mm, "mid": v(80.53, 25.79) * mm, "end": v(80.58, 24.41) * mm});
            skArc(sketch, "E231", {"start": v(82.5, 26.23) * mm, "mid": v(81.68, 26.98) * mm, "end": v(80.58, 27.16) * mm});
            skArc(sketch, "E232", {"start": v(82.5, 26.23) * mm, "mid": v(82.74, 20.57) * mm, "end": v(83.61, 14.98) * mm});
            skArc(sketch, "E233", {"start": v(83.61, 14.98) * mm, "mid": v(83.75, 14.25) * mm, "end": v(83.9, 13.54) * mm});
            skArc(sketch, "E234", {"start": v(83.9, 13.54) * mm, "mid": v(82.81, 13.5) * mm, "end": v(82.02, 12.75) * mm});
            skArc(sketch, "E235", {"start": v(82.02, 12.75) * mm, "mid": v(81.83, 13.3) * mm, "end": v(81.35, 13.62) * mm});
            skArc(sketch, "E236", {"start": v(81.35, 13.62) * mm, "mid": v(80.4, 13.78) * mm, "end": v(79.42, 13.66) * mm});
            skArc(sketch, "E237", {"start": v(79.42, 13.66) * mm, "mid": v(78.75, 13.37) * mm, "end": v(78.2, 12.89) * mm});
            skArc(sketch, "E238", {"start": v(78.2, 12.89) * mm, "mid": v(78.03, 12.25) * mm, "end": v(78.2, 11.6) * mm});
            skArc(sketch, "E239", {"start": v(78.2, 11.6) * mm, "mid": v(78.77, 10.8) * mm, "end": v(79.51, 10.13) * mm});
            skArc(sketch, "E240", {"start": v(79.51, 10.13) * mm, "mid": v(80.1, 9.77) * mm, "end": v(80.75, 9.6) * mm});
            skArc(sketch, "E241", {"start": v(80.75, 9.6) * mm, "mid": v(81.94, 9.74) * mm, "end": v(83.07, 10.14) * mm});
            skArc(sketch, "E242", {"start": v(82.62, 10.9) * mm, "mid": v(82.83, 10.5) * mm, "end": v(83.07, 10.14) * mm});
            skArc(sketch, "E243", {"start": v(82.62, 10.9) * mm, "mid": v(83.95, 10.73) * mm, "end": v(84.87, 11.7) * mm});
            skArc(sketch, "E244", {"start": v(84.87, 11.7) * mm, "mid": v(85.43, 11.6) * mm, "end": v(86, 11.7) * mm});
            skArc(sketch, "E245", {"start": v(86, 11.7) * mm, "mid": v(86.17, 11.87) * mm, "end": v(86.28, 12.08) * mm});
            skArc(sketch, "E246", {"start": v(85.27, 9.76) * mm, "mid": v(86.04, 10.8) * mm, "end": v(86.28, 12.08) * mm});
            skArc(sketch, "E247", {"start": v(82.61, 8.4) * mm, "mid": v(84.05, 8.87) * mm, "end": v(85.27, 9.76) * mm});
            skArc(sketch, "E248", {"start": v(79.55, 8.67) * mm, "mid": v(81.06, 8.36) * mm, "end": v(82.61, 8.4) * mm});
            skArc(sketch, "E249", {"start": v(77.14, 10.35) * mm, "mid": v(78.24, 9.36) * mm, "end": v(79.55, 8.67) * mm});
            skLineSegment(sketch, "E250", {"start": v(69.68, 9.13) * mm, "end": v(69.6, 8.71) * mm});
            skArc(sketch, "E251", {"start": v(76.23, 13.55) * mm, "mid": v(76.43, 11.88) * mm, "end": v(77.14, 10.35) * mm});
            skArc(sketch, "E252", {"start": v(77.12, 14.8) * mm, "mid": v(76.7, 14.4) * mm, "end": v(76.38, 13.92) * mm});
            skArc(sketch, "E253", {"start": v(76.86, 15.35) * mm, "mid": v(76.62, 14.64) * mm, "end": v(76.38, 13.92) * mm});
            skCircle(sketch, "E254.0", {"center": v(83.45, 12.12) * mm, "radius": 0.65 * mm});
            skLineSegment(sketch, "E255.trimOffspring", {"start": v(81.93, 13.12) * mm, "end": v(82.27, 13.12) * mm});
            skLineSegment(sketch, "E256.trimOffspring", {"start": v(76.1, 13.12) * mm, "end": v(76.23, 13.12) * mm});
            skSolve(sketch);
        }
        {
            var Q0;
            Q0=makeQuery(id+"F14.imprint","IMPRINT",FACE,{"disambiguationData":[TD([[makeQuery(id+"F14.imprint","IMPRINT",EDGE,{"derivedFrom":sQuery(id+"F14.wireOp",EDGE,"E189")}),-1.0]])]});
            var Q1;
            Q1=makeQuery(id+"F14.imprint","IMPRINT",FACE,{"disambiguationData":[TD([[makeQuery(id+"F14.imprint","IMPRINT",EDGE,{"derivedFrom":sQuery(id+"F14.wireOp",EDGE,"2de26a2a-8521-4cd1-8dbb-5edd335c7e13")}),1.0]])]});
            extrude(context, id + "F15", {"entities" : qUnion([Q0, Q1]), "operationType" : NewBodyOperationType.REMOVE, "oppositeDirection" : true, "depth" : 3 * mm});
        }
        {
            var Q0;
            Q0=makeQuery(id+"F1.opExtrude","SWEPT_EDGE",EDGE,{"disambiguationData":[OSD([sQuery(id+"F0.wireOp",EDGE,"E4"),sQuery(id+"F0.wireOp",EDGE,"E36")])]});
            fillet(context, id + "F16", {"entities" : qUnion([Q0]), "radius" : 5 * mm, "tangentPropagation" : true, "allowEdgeOverflow" : false});
        }
    });
